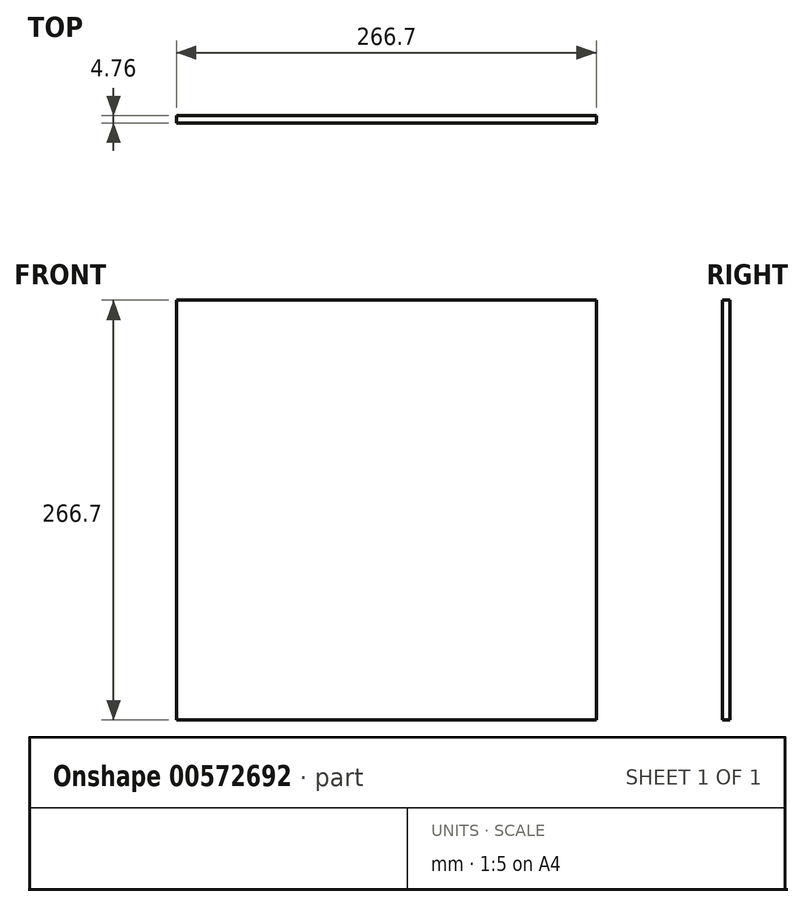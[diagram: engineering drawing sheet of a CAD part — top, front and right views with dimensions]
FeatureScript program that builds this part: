
annotation { "Feature Type Name" : "Feature", "Feature Type Description" : "" }
export const myFeature = defineFeature(function(context is Context, id is Id, definition is map)
    precondition{}
    {
        {
            var Q0;
            Q0=qCreatedBy(makeId("Front.planeOp"),FACE);
            var sketch = newSketch(context, id + "F0", { "sketchPlane" : qUnion([Q0])});
            skLineSegment(sketch, "E0.bottom", {"start": v(0, 0) * mm, "end": v(266.7, 0) * mm});
            skLineSegment(sketch, "E0.top", {"start": v(0, 266.7) * mm, "end": v(266.7, 266.7) * mm});
            skLineSegment(sketch, "E0.left", {"start": v(0, 0) * mm, "end": v(0, 266.7) * mm});
            skLineSegment(sketch, "E0.right", {"start": v(266.7, 0) * mm, "end": v(266.7, 266.7) * mm});
            skSolve(sketch);
        }
        {
            var Q0;
            Q0 = qSketchRegion(id + "F0", true);
            extrude(context, id + "F1", {"entities" : qUnion([Q0]), "oppositeDirection" : true, "depth" : 4.76 * mm, "offsetDistance" : 25.4 * mm});
        }
    });
